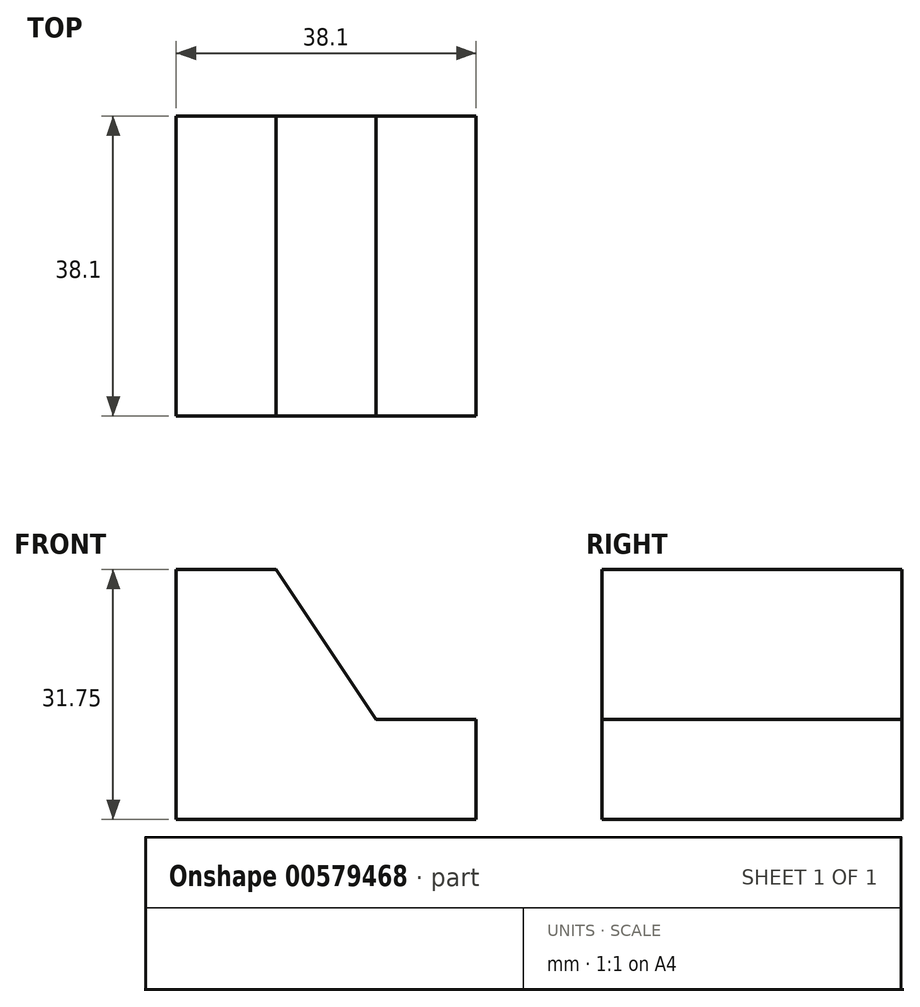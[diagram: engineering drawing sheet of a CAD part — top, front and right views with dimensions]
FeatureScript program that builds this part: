
annotation { "Feature Type Name" : "Feature", "Feature Type Description" : "" }
export const myFeature = defineFeature(function(context is Context, id is Id, definition is map)
    precondition{}
    {
        {
            var Q0;
            Q0=qCreatedBy(makeId("Front.planeOp"),FACE);
            var sketch = newSketch(context, id + "F0", { "sketchPlane" : qUnion([Q0])});
            skLineSegment(sketch, "E0", {"start": v(-42.56, 31.75) * mm, "end": v(-42.56, 0) * mm});
            skLineSegment(sketch, "E1", {"start": v(-42.56, 0) * mm, "end": v(-4.46, 0) * mm});
            skLineSegment(sketch, "E2", {"start": v(-4.46, 0) * mm, "end": v(-4.46, 12.7) * mm});
            skLineSegment(sketch, "E3", {"start": v(-4.46, 12.7) * mm, "end": v(-17.16, 12.7) * mm});
            skLineSegment(sketch, "E4", {"start": v(-17.16, 12.7) * mm, "end": v(-29.86, 31.75) * mm});
            skLineSegment(sketch, "E5", {"start": v(-29.86, 31.75) * mm, "end": v(-42.56, 31.75) * mm});
            skSolve(sketch);
        }
        {
            var Q0;
            Q0 = qSketchRegion(id + "F0", true);
            extrude(context, id + "F1", {"entities" : qUnion([Q0]), "depth" : 38.1 * mm, "offsetDistance" : 25.4 * mm});
        }
    });
